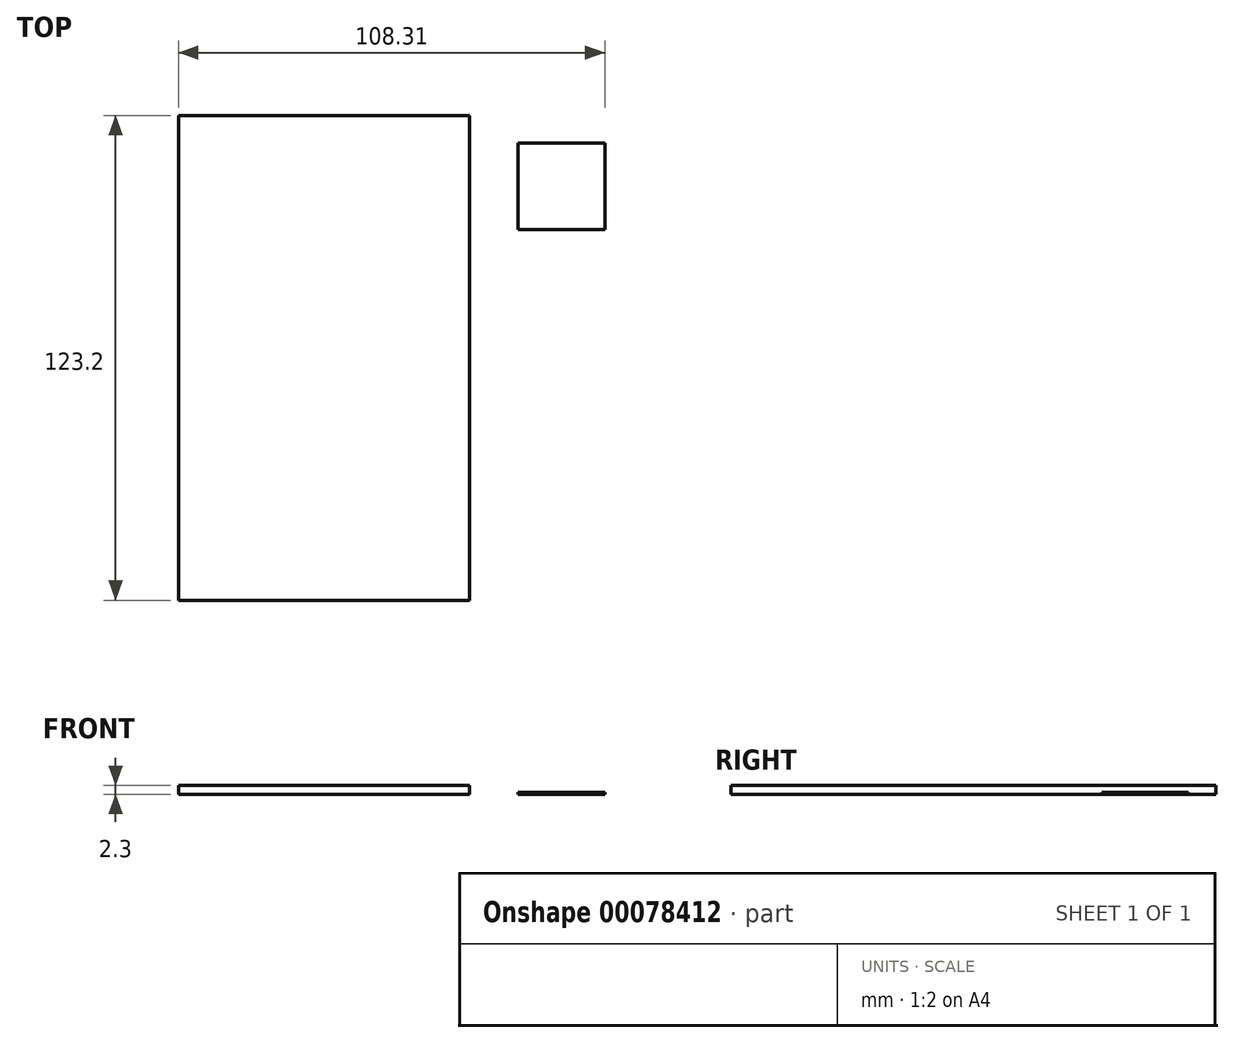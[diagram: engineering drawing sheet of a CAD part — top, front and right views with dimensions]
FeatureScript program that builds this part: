
annotation { "Feature Type Name" : "Feature", "Feature Type Description" : "" }
export const myFeature = defineFeature(function(context is Context, id is Id, definition is map)
    precondition{}
    {
        {
            var Q0;
            Q0=qCreatedBy(makeId("Top.planeOp"),FACE);
            var sketch = newSketch(context, id + "F0", { "sketchPlane" : qUnion([Q0])});
            skLineSegment(sketch, "E0.bottom", {"start": v(0, 61.6) * mm, "end": v(-37, 61.6) * mm});
            skLineSegment(sketch, "E0.right", {"start": v(-37, 61.6) * mm, "end": v(-37, 0) * mm});
            skLineSegment(sketch, "E1.MirrorCS", {"start": v(0, 61.6) * mm, "end": v(37, 61.6) * mm});
            skLineSegment(sketch, "E2.MirrorCS", {"start": v(37, 61.6) * mm, "end": v(37, 0) * mm});
            skLineSegment(sketch, "E3.MirrorCS", {"start": v(-37, -61.6) * mm, "end": v(-37, 0) * mm});
            skLineSegment(sketch, "E4.MirrorCS", {"start": v(0, -61.6) * mm, "end": v(-37, -61.6) * mm});
            skLineSegment(sketch, "E5.MirrorCS", {"start": v(0, -61.6) * mm, "end": v(37, -61.6) * mm});
            skLineSegment(sketch, "E6.MirrorCS", {"start": v(37, -61.6) * mm, "end": v(37, 0) * mm});
            skLineSegment(sketch, "E7.bottom", {"start": v(49.31, 54.63) * mm, "end": v(71.31, 54.63) * mm});
            skLineSegment(sketch, "E7.top", {"start": v(49.31, 32.63) * mm, "end": v(71.31, 32.63) * mm});
            skLineSegment(sketch, "E7.left", {"start": v(49.31, 54.63) * mm, "end": v(49.31, 32.63) * mm});
            skLineSegment(sketch, "E7.right", {"start": v(71.31, 54.63) * mm, "end": v(71.31, 32.63) * mm});
            skSolve(sketch);
        }
        {
            var Q0;
            Q0=makeQuery(id+"F0.imprint","IMPRINT",FACE,{"disambiguationData":[TD([[makeQuery(id+"F0.imprint","IMPRINT",EDGE,{"derivedFrom":sQuery(id+"F0.wireOp",EDGE,"E0.bottom")}),1.0]])]});
            extrude(context, id + "F1", {"entities" : qUnion([Q0]), "depth" : 2.3 * mm, "offsetDistance" : 25 * mm});
        }
        {
            var Q0;
            Q0=makeQuery(id+"F0.imprint","IMPRINT",FACE,{"disambiguationData":[TD([[makeQuery(id+"F0.imprint","IMPRINT",EDGE,{"derivedFrom":sQuery(id+"F0.wireOp",EDGE,"E7.bottom")}),-1.0]])]});
            extrude(context, id + "F2", {"entities" : qUnion([Q0]), "depth" : .5 * mm, "offsetDistance" : 25 * mm});
        }
    });
